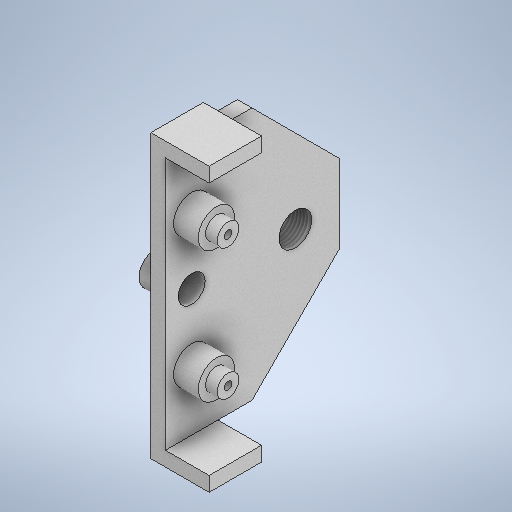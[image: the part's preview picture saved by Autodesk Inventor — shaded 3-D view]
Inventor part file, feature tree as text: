
AUTODESK INVENTOR PART (.ipt)
format: ipt  version: 2025.2 (Build 292293000, 293)  size: 388,096 bytes
history: native  units: in
note: dims shown in document units (in); Inventor stores cm internally (conversion verified against a paired STEP export)
features: extrude x6, other x5, plane x1, hole x1, sketch x1
ambient origin geometry x8: Origin, YZ Plane, XZ Plane, XY Plane, X Axis, Y Axis, Z Axis, Center Point
bodies: Volumenkörper1 (feature_tree)
feature tree (14):
  other  "Skelett_Laufkatze.ipt"
  extrude  "Grundplatte"  Depth=0.3937in TaperAngle=0.0deg
  extrude  "Wellenöffnung_für_Kettenzug"  Depth=0.3937in TaperAngle=0.0deg
  extrude  "Laufradaufhängung_1"  Depth=0.3937in TaperAngle=0.0deg
  extrude  "Laufradaufhängung_2"  Depth=0.3937in TaperAngle=0.0deg
  extrude  "Schutzwände"  Depth=0.3937in TaperAngle=0.0deg
  extrude  "Schraubbolzenöffnung"  Depth=0.3937in TaperAngle=0.0deg
  other  "Schraubbolzengewinde"
  plane  "Arbeitsebene1"
  hole  "Bohrung1"  [1 undecoded]
  other  "Fuehrungsplatte_seite_Kettenzug"
  other  "Fuehrungsplatte_Laufradaufhängung_Kettenzug"
  other  "Fuehrungsplatte_Schraubbolzen_Kettenzug"
  sketch  "Skizze4"  dims[d0=0.3937in d1=0.3937in d2=0.0in d3=0.3937in d4=0.0in d5=0.3937in d6=0.0in d7=0.3937in d8=0.0in d9=0.3937in d10=0.0in d11=0.3937in d12=0.0in d13=1.9685in d14=0.0in d15=0.0in d16=0.4192in d17=0.9449in d18=0.1575in d19=0.0787in d20=90.0deg d21=1.189in d22=0.8108in]
note: 1 required parameter value undecoded (feature->parameter linkage not recoverable at this tier; creation-order binding heuristic only, values carry confidence <= 0.55)
